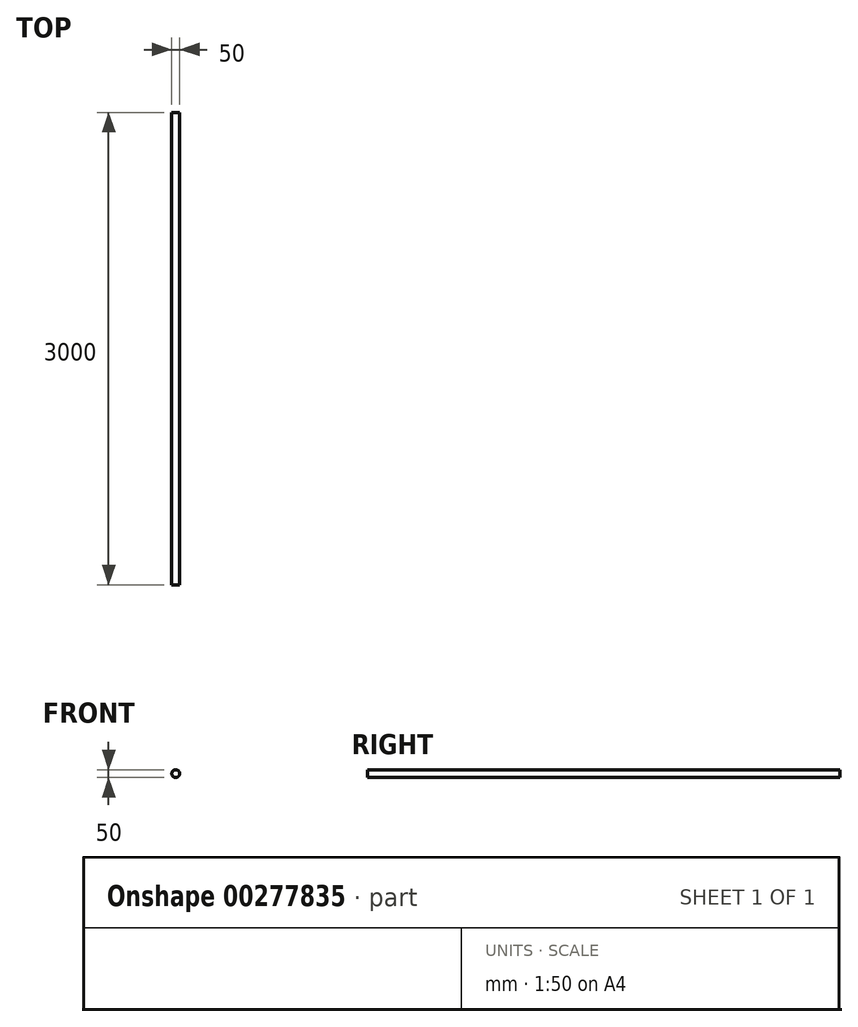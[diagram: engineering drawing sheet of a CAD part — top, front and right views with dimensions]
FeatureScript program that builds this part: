
annotation { "Feature Type Name" : "Feature", "Feature Type Description" : "" }
export const myFeature = defineFeature(function(context is Context, id is Id, definition is map)
    precondition{}
    {
        {
            var Q0;
            Q0=qCreatedBy(makeId("Front.planeOp"),FACE);
            var sketch = newSketch(context, id + "F0", { "sketchPlane" : qUnion([Q0])});
            skCircle(sketch, "E0", {"center": v(0, 0) * mm, "radius": 25 * mm});
            skSolve(sketch);
        }
        {
            var Q0;
            Q0=makeQuery(id+"F0.imprint","IMPRINT",FACE,{"disambiguationData":[TD([[makeQuery(id+"F0.imprint","IMPRINT",EDGE,{"derivedFrom":sQuery(id+"F0.wireOp",EDGE,"E0")}),1.0]])]});
            extrude(context, id + "F1", {"entities" : qUnion([Q0]), "oppositeDirection" : true, "depth" : 3000 * mm});
        }
    });
